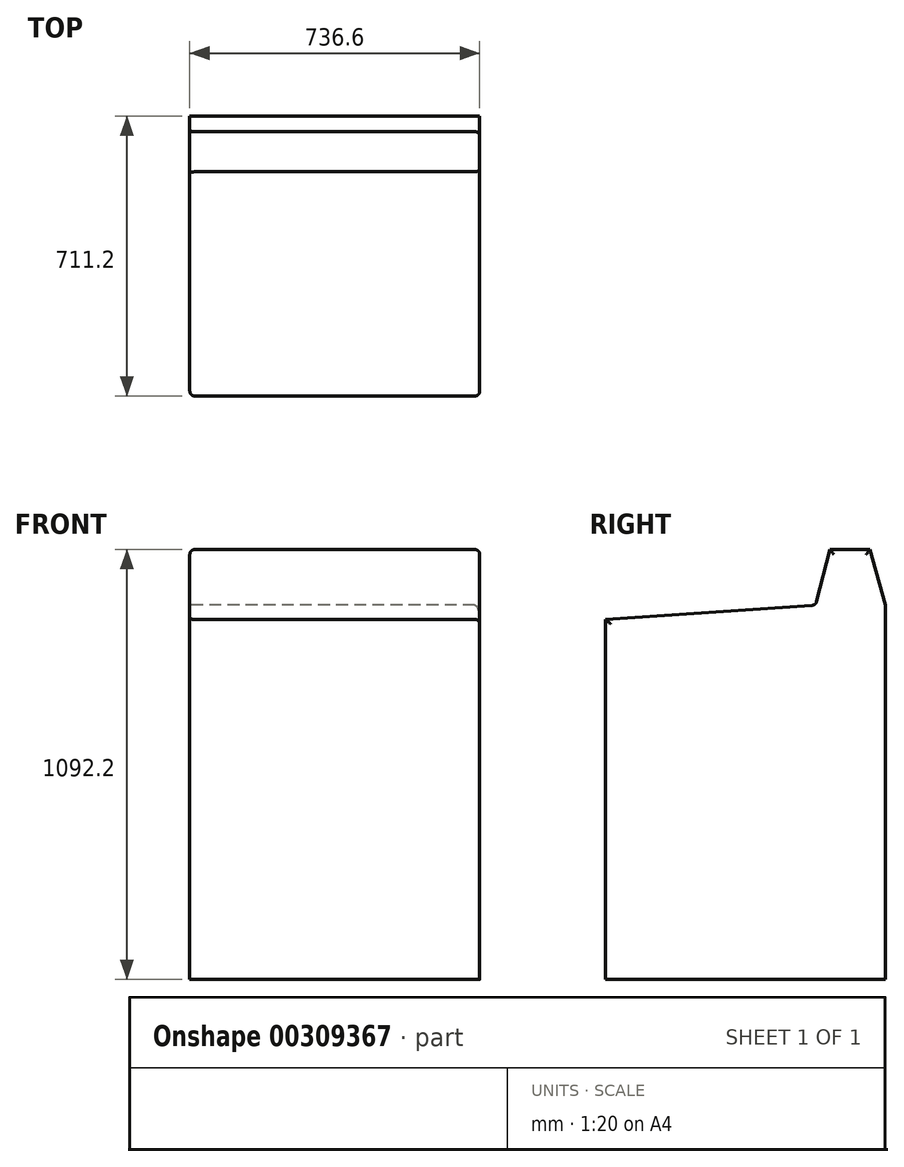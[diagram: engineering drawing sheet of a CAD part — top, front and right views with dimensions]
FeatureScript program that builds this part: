
annotation { "Feature Type Name" : "Feature", "Feature Type Description" : "" }
export const myFeature = defineFeature(function(context is Context, id is Id, definition is map)
    precondition{}
    {
        {
            var Q0;
            Q0=qCreatedBy(makeId("Top.planeOp"),FACE);
            var sketch = newSketch(context, id + "F0", { "sketchPlane" : qUnion([Q0])});
            skLineSegment(sketch, "E0.bottom", {"start": v(0, 0) * mm, "end": v(736.6, 0) * mm});
            skLineSegment(sketch, "E0.top", {"start": v(0, -711.2) * mm, "end": v(736.6, -711.2) * mm});
            skLineSegment(sketch, "E0.left", {"start": v(0, 0) * mm, "end": v(0, -711.2) * mm});
            skLineSegment(sketch, "E0.right", {"start": v(736.6, 0) * mm, "end": v(736.6, -711.2) * mm});
            skSolve(sketch);
        }
        {
            var Q0;
            Q0=qSketchRegion(id+"F0",true);
            extrude(context, id + "F1", {"entities" : qUnion([Q0]), "depth" : 1092.2 * mm});
        }
        {
            var Q0;
            Q0=makeQuery(id+"F1.opExtrude","SWEPT_FACE",FACE,{"disambiguationData":[OSD([sQuery(id+"F0.wireOp",EDGE,"E0.left")])]});
            var sketch = newSketch(context, id + "F2", { "sketchPlane" : qUnion([Q0])});
            skLineSegment(sketch, "E1", {"start": v(0, 950.97) * mm, "end": v(39.62, 1092.2) * mm});
            skLineSegment(sketch, "E2", {"start": v(39.62, 1092.2) * mm, "end": v(141.55, 1092.2) * mm});
            skLineSegment(sketch, "E3", {"start": v(141.55, 1092.2) * mm, "end": v(177.52, 950.97) * mm});
            skLineSegment(sketch, "E4", {"start": v(177.52, 950.97) * mm, "end": v(711.2, 915) * mm});
            skSolve(sketch);
        }
        {
            var Q0;
            Q0=qSketchRegion(id+"F2",true);
            var Q1;
            {var subQ0=sQuery(id+"F2.wireOp",EDGE,"E3");Q1=makeQuery(id+"F2.imprint","IMPRINT",FACE,{"disambiguationData":[TD([[makeQuery(id+"F2.imprint","IMPRINT",EDGE,{"derivedFrom":subQ0}),1.0]])]});}
            var Q2;
            {var subQ0=sQuery(id+"F2.wireOp",EDGE,"E1");Q2=makeQuery(id+"F2.imprint","IMPRINT",FACE,{"disambiguationData":[TD([[makeQuery(id+"F2.imprint","IMPRINT",EDGE,{"derivedFrom":subQ0}),1.0]])]});}
            extrude(context, id + "F3", {"entities" : qUnion([Q0, Q1, Q2]), "operationType" : NewBodyOperationType.REMOVE, "endBound" : BoundingType.THROUGH_ALL, "oppositeDirection" : true, "depth" : 25.4 * mm});
        }
        {
            var Q0;
            Q0=makeQuery(id+"F1.opExtrude","SWEPT_EDGE",EDGE,{"disambiguationData":[OSD([sQuery(id+"F0.wireOp",EDGE,"E0.top"),sQuery(id+"F0.wireOp",EDGE,"E0.left")])]});
            var Q1;
            Q1=makeQuery(id+"F1.opExtrude","SWEPT_EDGE",EDGE,{"disambiguationData":[OSD([sQuery(id+"F0.wireOp",EDGE,"E0.top"),sQuery(id+"F0.wireOp",EDGE,"E0.right")])]});
            var Q2;
            Q2=makeQuery(id+"F3.boolean.opBoolean","COPY",EDGE,{"derivedFrom":makeQuery(id+"F3.opExtrude","SWEPT_EDGE",EDGE,{"disambiguationData":[OSD([sQuery(id+"F0.wireOp",EDGE,"E0.top"),sQuery(id+"F0.wireOp",EDGE,"E0.left"),sQuery(id+"F2.wireOp",EDGE,"E4")])]})});
            var Q3;
            Q3=makeQuery(id+"F3.boolean.opBoolean","COPY",EDGE,{"derivedFrom":makeQuery(id+"F3.opExtrude","CAP_EDGE",EDGE,{"disambiguationData":[OSD([sQuery(id+"F2.wireOp",EDGE,"E4")])],"isStart":true})});
            var Q4;
            Q4=makeQuery(id+"F3.boolean.opBoolean","INTERSECT",EDGE,{"derivedFrom":[makeQuery(id+"F1.opExtrude","SWEPT_FACE",FACE,{"disambiguationData":[OSD([sQuery(id+"F0.wireOp",EDGE,"E0.right")])]}),makeQuery(id+"F3.opExtrude","SWEPT_FACE",FACE,{"disambiguationData":[OSD([sQuery(id+"F2.wireOp",EDGE,"E4")])]})]});
            var Q5;
            Q5=makeQuery(id+"F3.boolean.opBoolean","COPY",EDGE,{"derivedFrom":makeQuery(id+"F3.opExtrude","SWEPT_EDGE",EDGE,{"disambiguationData":[OSD([sQuery(id+"F2.wireOp",EDGE,"E3"),sQuery(id+"F2.wireOp",EDGE,"E4")])]})});
            var Q6;
            Q6=makeQuery(id+"F3.boolean.opBoolean","COPY",EDGE,{"derivedFrom":makeQuery(id+"F3.opExtrude","SWEPT_EDGE",EDGE,{"disambiguationData":[OSD([sQuery(id+"F0.wireOp",EDGE,"E0.left"),sQuery(id+"F2.wireOp",EDGE,"E2"),sQuery(id+"F2.wireOp",EDGE,"E3")])]})});
            var Q7;
            Q7=makeQuery(id+"F3.boolean.opBoolean","COPY",EDGE,{"derivedFrom":makeQuery(id+"F3.opExtrude","SWEPT_EDGE",EDGE,{"disambiguationData":[OSD([sQuery(id+"F0.wireOp",EDGE,"E0.left"),sQuery(id+"F2.wireOp",EDGE,"E1"),sQuery(id+"F2.wireOp",EDGE,"E2")])]})});
            var Q8;
            Q8=makeQuery(id+"F3.boolean.opBoolean","COPY",EDGE,{"derivedFrom":makeQuery(id+"F3.opExtrude","CAP_EDGE",EDGE,{"disambiguationData":[OSD([sQuery(id+"F2.wireOp",EDGE,"E3")])],"isStart":true})});
            var Q9;
            Q9=makeQuery(id+"F3.boolean.opBoolean","INTERSECT",EDGE,{"derivedFrom":[makeQuery(id+"F1.opExtrude","SWEPT_FACE",FACE,{"disambiguationData":[OSD([sQuery(id+"F0.wireOp",EDGE,"E0.right")])]}),makeQuery(id+"F3.opExtrude","SWEPT_FACE",FACE,{"disambiguationData":[OSD([sQuery(id+"F2.wireOp",EDGE,"E3")])]})]});
            var Q10;
            Q10=makeQuery(id+"F3.boolean.opBoolean","COPY",EDGE,{"derivedFrom":makeQuery(id+"F3.opExtrude","CAP_EDGE",EDGE,{"disambiguationData":[OSD([sQuery(id+"F2.wireOp",EDGE,"E1")])],"isStart":true})});
            var Q11;
            Q11=makeQuery(id+"F1.opExtrude","CAP_EDGE",EDGE,{"disambiguationData":[OSD([sQuery(id+"F0.wireOp",EDGE,"E0.right")])],"isStart":false});
            var Q12;
            Q12=makeQuery(id+"F3.boolean.opBoolean","INTERSECT",EDGE,{"derivedFrom":[makeQuery(id+"F1.opExtrude","SWEPT_FACE",FACE,{"disambiguationData":[OSD([sQuery(id+"F0.wireOp",EDGE,"E0.right")])]}),makeQuery(id+"F3.opExtrude","SWEPT_FACE",FACE,{"disambiguationData":[OSD([sQuery(id+"F2.wireOp",EDGE,"E1")])]})]});
            var Q13;
            Q13=makeQuery(id+"F1.opExtrude","CAP_EDGE",EDGE,{"disambiguationData":[OSD([sQuery(id+"F0.wireOp",EDGE,"E0.left")])],"isStart":false});
            fillet(context, id + "F4", {"entities" : qUnion([Q0, Q1, Q2, Q3, Q4, Q5, Q6, Q7, Q8, Q9, Q10, Q11, Q12, Q13]), "radius" : 12.7 * mm, "tangentPropagation" : true, "allowEdgeOverflow" : false});
        }
    });
